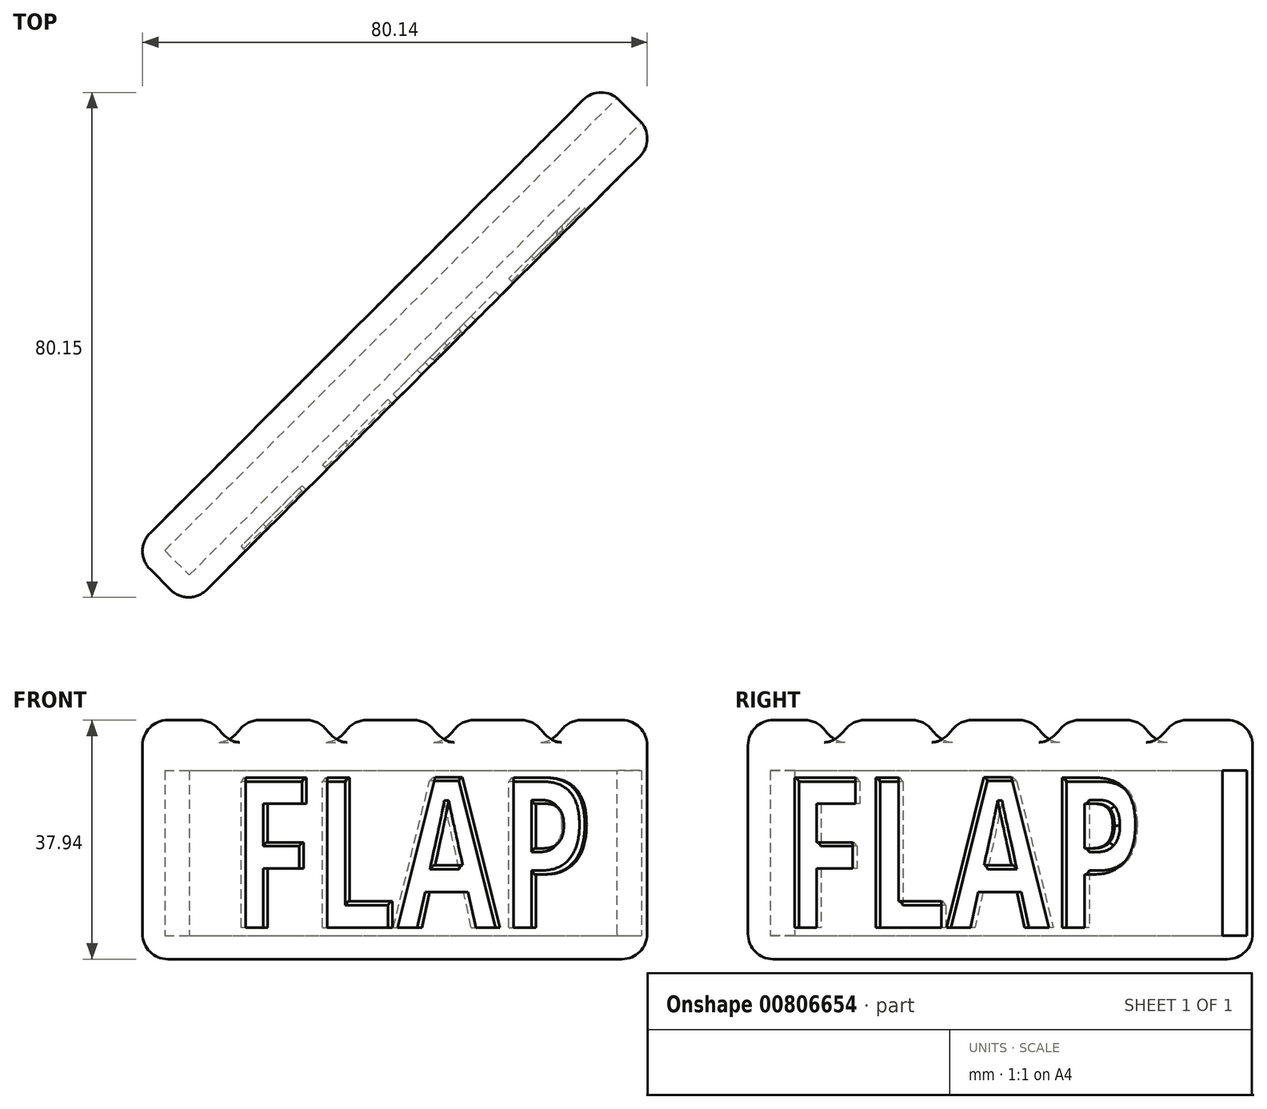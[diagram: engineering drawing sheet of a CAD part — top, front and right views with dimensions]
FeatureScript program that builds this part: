
annotation { "Feature Type Name" : "Feature", "Feature Type Description" : "" }
export const myFeature = defineFeature(function(context is Context, id is Id, definition is map)
    precondition{}
    {
        {
            assignVariable(context, id + "F0", {"name" : "tolerance", "anyValue" : 0.4 * mm});
        }
        {
            var Q0;
            Q0=qCreatedBy(makeId("Right.planeOp"),FACE);
            var sketch = newSketch(context, id + "F1", { "sketchPlane" : qUnion([Q0])});
            skLineSegment(sketch, "E0.bottom", {"start": v(0, 0) * mm, "end": v(152.4, 0) * mm});
            skLineSegment(sketch, "E0.top", {"start": v(0, 26.2) * mm, "end": v(152.4, 26.2) * mm});
            skLineSegment(sketch, "E0.left", {"start": v(0, 0) * mm, "end": v(0, 26.2) * mm});
            skLineSegment(sketch, "E0.right", {"start": v(152.4, 0) * mm, "end": v(152.4, 26.2) * mm});
            skSolve(sketch);
        }
        {
            var Q0;
            Q0=makeQuery(id+"F1.imprint","IMPRINT",FACE,{"disambiguationData":[TD([[makeQuery(id+"F1.imprint","IMPRINT",EDGE,{"derivedFrom":sQuery(id+"F1.wireOp",EDGE,"E0.bottom")}),1.0]])]});
            extrude(context, id + "F2", {"entities" : qUnion([Q0]), "endBound" : BoundingType.SYMMETRIC, "depth" : 4.7 * mm + 2 * getVariable(context, 'tolerance'), "offsetDistance" : 25.4 * mm});
        }
        {
            var Q0;
            Q0=qCreatedBy(makeId("Right.planeOp"),FACE);
            var sketch = newSketch(context, id + "F3", { "sketchPlane" : qUnion([Q0])});
            skLineSegment(sketch, "E1.bottom", {"start": v(-3.73, 29.95) * mm, "end": v(101.6, 29.95) * mm});
            skLineSegment(sketch, "E1.right", {"start": v(101.6, 29.95) * mm, "end": v(101.6, -8) * mm});
            skLineSegment(sketch, "E2.0.0", {"start": v(152.4, 26.2) * mm, "end": v(0, 26.2) * mm, "construction": true});
            skLineSegment(sketch, "E2.0.1", {"start": v(0, 26.2) * mm, "end": v(0, 0) * mm, "construction": true});
            skLineSegment(sketch, "E2.0.2", {"start": v(0, 0) * mm, "end": v(152.4, 0) * mm, "construction": true});
            skLineSegment(sketch, "E2.0.3", {"start": v(152.4, 0) * mm, "end": v(152.4, 26.2) * mm, "construction": true});
            skLineSegment(sketch, "E3", {"start": v(-3.73, 29.95) * mm, "end": v(-3.73, -8) * mm});
            skLineSegment(sketch, "E4", {"start": v(-3.73, -8) * mm, "end": v(4.36, -8) * mm});
            skLineSegment(sketch, "E5", {"start": v(-3.73, -14) * mm, "end": v(101.6, -14) * mm, "construction": true});
            skArc(sketch, "E6.1.0.0", {"start": v(43.26, -8) * mm, "mid": v(35.86, -4.47) * mm, "end": v(28.46, -8) * mm});
            skLineSegment(sketch, "E6.1.0.1", {"start": v(20.37, -14) * mm, "end": v(125.7, -14) * mm, "construction": true});
            skArc(sketch, "E6.2.0.0", {"start": v(67.36, -8) * mm, "mid": v(59.96, -4.47) * mm, "end": v(52.56, -8) * mm});
            skLineSegment(sketch, "E6.2.0.1", {"start": v(44.47, -14) * mm, "end": v(149.8, -14) * mm, "construction": true});
            skArc(sketch, "E6.3.0.0", {"start": v(91.46, -8) * mm, "mid": v(84.06, -4.47) * mm, "end": v(76.66, -8) * mm});
            skLineSegment(sketch, "E6.3.0.1", {"start": v(68.57, -14) * mm, "end": v(173.9, -14) * mm, "construction": true});
            skLineSegment(sketch, "E6.direction1", {"start": v(11.76, -14) * mm, "end": v(35.86, -14) * mm, "construction": true});
            skArc(sketch, "E7.trimOffspring", {"start": v(19.16, -8) * mm, "mid": v(11.76, -4.48) * mm, "end": v(4.36, -8) * mm});
            skLineSegment(sketch, "E8.trimOffspring", {"start": v(19.16, -8) * mm, "end": v(28.46, -8) * mm});
            skLineSegment(sketch, "E9.trimOffspring", {"start": v(43.26, -8) * mm, "end": v(52.56, -8) * mm});
            skLineSegment(sketch, "E10.trimOffspring", {"start": v(91.46, -8) * mm, "end": v(101.6, -8) * mm});
            skLineSegment(sketch, "E11.trimOffspring", {"start": v(67.36, -8) * mm, "end": v(76.66, -8) * mm});
            skSolve(sketch);
        }
        {
            var Q0;
            Q0=makeQuery(id+"F3.imprint","IMPRINT",FACE,{"disambiguationData":[TD([[makeQuery(id+"F3.imprint","IMPRINT",EDGE,{"derivedFrom":sQuery(id+"F3.wireOp",EDGE,"E1.bottom")}),-1.0]])]});
            extrude(context, id + "F4", {"entities" : qUnion([Q0]), "endBound" : BoundingType.SYMMETRIC, "depth" : 12.7 * mm, "offsetDistance" : 25.4 * mm});
        }
        {
            var Q0;
            {var subQ0=sQuery(id+"F3.wireOp",EDGE,"E1.top");Q0=makeQuery(id+"F4.opExtrude","SWEPT_FACE",FACE,{"disambiguationData":[OSD([subQ0]),TDD([makeQuery(id+"F3.imprint","IMPRINT",EDGE,{"disambiguationData":[TD([[makeQuery(id+"F3.imprint","INTERSECT",VERTEX,{"disambiguationData":[OD(0.0)],"derivedFrom":[subQ0,sQuery(id+"F3.wireOp",EDGE,"ST85VybC-jDZY-28ir-gOz5-esfVJcpXRgd0")]}),-1.0]])],"derivedFrom":subQ0})])]});}
            var Q1;
            {var subQ0=sQuery(id+"F3.wireOp",EDGE,"E1.top");Q1=makeQuery(id+"F4.opExtrude","SWEPT_FACE",FACE,{"disambiguationData":[OSD([subQ0]),TDD([makeQuery(id+"F3.imprint","IMPRINT",EDGE,{"disambiguationData":[TD([[makeQuery(id+"F3.imprint","INTERSECT",VERTEX,{"disambiguationData":[OD(0.0)],"derivedFrom":[subQ0,sQuery(id+"F3.wireOp",EDGE,"1f6f91a6-61ac-4653-8395-83e8434b74c3.1.0.0")]}),-1.0]])],"derivedFrom":subQ0})])]});}
            var Q2;
            {var subQ0=sQuery(id+"F3.wireOp",EDGE,"E1.top");Q2=makeQuery(id+"F4.opExtrude","SWEPT_FACE",FACE,{"disambiguationData":[OSD([subQ0]),TDD([makeQuery(id+"F3.imprint","IMPRINT",EDGE,{"disambiguationData":[TD([[makeQuery(id+"F3.imprint","INTERSECT",VERTEX,{"disambiguationData":[OD(0.0)],"derivedFrom":[subQ0,sQuery(id+"F3.wireOp",EDGE,"1f6f91a6-61ac-4653-8395-83e8434b74c3.2.0.0")]}),-1.0]])],"derivedFrom":subQ0})])]});}
            var Q3;
            Q3=makeQuery(id+"F4.opExtrude","SWEPT_FACE",FACE,{"disambiguationData":[OSD([sQuery(id+"F3.wireOp",EDGE,"1f6f91a6-61ac-4653-8395-83e8434b74c3.3.0.0")])]});
            var Q4;
            Q4=makeQuery(id+"F4.opExtrude","SWEPT_FACE",FACE,{"disambiguationData":[OSD([sQuery(id+"F3.wireOp",EDGE,"1f6f91a6-61ac-4653-8395-83e8434b74c3.2.0.0")])]});
            var Q5;
            Q5=makeQuery(id+"F4.opExtrude","SWEPT_FACE",FACE,{"disambiguationData":[OSD([sQuery(id+"F3.wireOp",EDGE,"1f6f91a6-61ac-4653-8395-83e8434b74c3.1.0.0")])]});
            var Q6;
            Q6=makeQuery(id+"F4.opExtrude","SWEPT_FACE",FACE,{"disambiguationData":[OSD([sQuery(id+"F3.wireOp",EDGE,"ST85VybC-jDZY-28ir-gOz5-esfVJcpXRgd0")])]});
            var Q7;
            {var subQ0=sQuery(id+"F3.wireOp",EDGE,"E1.top");Q7=makeQuery(id+"F4.opExtrude","SWEPT_FACE",FACE,{"disambiguationData":[OSD([subQ0]),TDD([makeQuery(id+"F3.imprint","IMPRINT",EDGE,{"disambiguationData":[TD([[makeQuery(id+"F3.imprint","INTERSECT",VERTEX,{"derivedFrom":[subQ0,sQuery(id+"F3.wireOp",EDGE,"E1.left")]}),-1.0]])],"derivedFrom":subQ0})])]});}
            var Q8;
            {var subQ0=sQuery(id+"F3.wireOp",EDGE,"E1.top");Q8=makeQuery(id+"F4.opExtrude","SWEPT_FACE",FACE,{"disambiguationData":[OSD([subQ0]),TDD([makeQuery(id+"F3.imprint","IMPRINT",EDGE,{"disambiguationData":[TD([[makeQuery(id+"F3.imprint","INTERSECT",VERTEX,{"derivedFrom":[subQ0,sQuery(id+"F3.wireOp",EDGE,"E1.right")]}),1.0]])],"derivedFrom":subQ0})])]});}
            var Q9;
            Q9=makeQuery(id+"F4.opExtrude","SWEPT_FACE",FACE,{"disambiguationData":[OSD([sQuery(id+"F3.wireOp",EDGE,"E1.left")])]});
            var Q10;
            Q10=makeQuery(id+"F4.opExtrude","SWEPT_FACE",FACE,{"disambiguationData":[OSD([sQuery(id+"F3.wireOp",EDGE,"E1.bottom")])]});
            var Q11;
            Q11=makeQuery(id+"F4.opExtrude","SWEPT_FACE",FACE,{"disambiguationData":[OSD([sQuery(id+"F3.wireOp",EDGE,"E1.right")])]});
            var Q12;
            Q12=makeQuery(id+"F4.opExtrude","SWEPT_EDGE",EDGE,{"disambiguationData":[OSD([sQuery(id+"F3.wireOp",EDGE,"E6.3.0.0"),sQuery(id+"F3.wireOp",EDGE,"E10.trimOffspring")])]});
            var Q13;
            Q13=makeQuery(id+"F4.opExtrude","SWEPT_EDGE",EDGE,{"disambiguationData":[OSD([sQuery(id+"F3.wireOp",EDGE,"E6.3.0.0"),sQuery(id+"F3.wireOp",EDGE,"E11.trimOffspring")])]});
            var Q14;
            Q14=makeQuery(id+"F4.opExtrude","SWEPT_EDGE",EDGE,{"disambiguationData":[OSD([sQuery(id+"F3.wireOp",EDGE,"E6.2.0.0"),sQuery(id+"F3.wireOp",EDGE,"E11.trimOffspring")])]});
            var Q15;
            Q15=makeQuery(id+"F4.opExtrude","SWEPT_EDGE",EDGE,{"disambiguationData":[OSD([sQuery(id+"F3.wireOp",EDGE,"E6.2.0.0"),sQuery(id+"F3.wireOp",EDGE,"E9.trimOffspring")])]});
            var Q16;
            Q16=makeQuery(id+"F4.opExtrude","SWEPT_EDGE",EDGE,{"disambiguationData":[OSD([sQuery(id+"F3.wireOp",EDGE,"E6.1.0.0"),sQuery(id+"F3.wireOp",EDGE,"E9.trimOffspring")])]});
            var Q17;
            Q17=makeQuery(id+"F4.opExtrude","SWEPT_EDGE",EDGE,{"disambiguationData":[OSD([sQuery(id+"F3.wireOp",EDGE,"E6.1.0.0"),sQuery(id+"F3.wireOp",EDGE,"E8.trimOffspring")])]});
            var Q18;
            Q18=makeQuery(id+"F4.opExtrude","SWEPT_EDGE",EDGE,{"disambiguationData":[OSD([sQuery(id+"F3.wireOp",EDGE,"E7.trimOffspring"),sQuery(id+"F3.wireOp",EDGE,"E8.trimOffspring")])]});
            var Q19;
            Q19=makeQuery(id+"F4.opExtrude","SWEPT_EDGE",EDGE,{"disambiguationData":[OSD([sQuery(id+"F3.wireOp",EDGE,"E4"),sQuery(id+"F3.wireOp",EDGE,"E7.trimOffspring")])]});
            var Q20;
            Q20=makeQuery(id+"F4.opExtrude","CAP_EDGE",EDGE,{"disambiguationData":[OSD([sQuery(id+"F3.wireOp",EDGE,"E7.trimOffspring")])],"isStart":false});
            var Q21;
            Q21=makeQuery(id+"F4.opExtrude","CAP_EDGE",EDGE,{"disambiguationData":[OSD([sQuery(id+"F3.wireOp",EDGE,"E6.1.0.0")])],"isStart":false});
            var Q22;
            Q22=makeQuery(id+"F4.opExtrude","CAP_EDGE",EDGE,{"disambiguationData":[OSD([sQuery(id+"F3.wireOp",EDGE,"E6.2.0.0")])],"isStart":false});
            var Q23;
            Q23=makeQuery(id+"F4.opExtrude","CAP_EDGE",EDGE,{"disambiguationData":[OSD([sQuery(id+"F3.wireOp",EDGE,"E6.3.0.0")])],"isStart":false});
            var Q24;
            Q24=makeQuery(id+"F4.opExtrude","CAP_EDGE",EDGE,{"disambiguationData":[OSD([sQuery(id+"F3.wireOp",EDGE,"E6.3.0.0")])],"isStart":true});
            var Q25;
            Q25=makeQuery(id+"F4.opExtrude","CAP_EDGE",EDGE,{"disambiguationData":[OSD([sQuery(id+"F3.wireOp",EDGE,"E6.2.0.0")])],"isStart":true});
            var Q26;
            Q26=makeQuery(id+"F4.opExtrude","CAP_EDGE",EDGE,{"disambiguationData":[OSD([sQuery(id+"F3.wireOp",EDGE,"E10.trimOffspring")])],"isStart":true});
            var Q27;
            Q27=makeQuery(id+"F4.opExtrude","CAP_EDGE",EDGE,{"disambiguationData":[OSD([sQuery(id+"F3.wireOp",EDGE,"E9.trimOffspring")])],"isStart":true});
            var Q28;
            Q28=makeQuery(id+"F4.opExtrude","CAP_EDGE",EDGE,{"disambiguationData":[OSD([sQuery(id+"F3.wireOp",EDGE,"E6.1.0.0")])],"isStart":true});
            var Q29;
            Q29=makeQuery(id+"F4.opExtrude","CAP_EDGE",EDGE,{"disambiguationData":[OSD([sQuery(id+"F3.wireOp",EDGE,"E8.trimOffspring")])],"isStart":true});
            var Q30;
            Q30=makeQuery(id+"F4.opExtrude","CAP_EDGE",EDGE,{"disambiguationData":[OSD([sQuery(id+"F3.wireOp",EDGE,"E7.trimOffspring")])],"isStart":true});
            var Q31;
            Q31=makeQuery(id+"F4.opExtrude","CAP_EDGE",EDGE,{"disambiguationData":[OSD([sQuery(id+"F3.wireOp",EDGE,"E4")])],"isStart":true});
            var Q32;
            Q32=makeQuery(id+"F4.opExtrude","CAP_EDGE",EDGE,{"disambiguationData":[OSD([sQuery(id+"F3.wireOp",EDGE,"E11.trimOffspring")])],"isStart":true});
            var Q33;
            Q33=makeQuery(id+"F4.opExtrude","CAP_EDGE",EDGE,{"disambiguationData":[OSD([sQuery(id+"F3.wireOp",EDGE,"E11.trimOffspring")])],"isStart":false});
            var Q34;
            Q34=makeQuery(id+"F4.opExtrude","CAP_EDGE",EDGE,{"disambiguationData":[OSD([sQuery(id+"F3.wireOp",EDGE,"E9.trimOffspring")])],"isStart":false});
            var Q35;
            Q35=makeQuery(id+"F4.opExtrude","CAP_EDGE",EDGE,{"disambiguationData":[OSD([sQuery(id+"F3.wireOp",EDGE,"E8.trimOffspring")])],"isStart":false});
            var Q36;
            Q36=makeQuery(id+"F4.opExtrude","CAP_EDGE",EDGE,{"disambiguationData":[OSD([sQuery(id+"F3.wireOp",EDGE,"E4")])],"isStart":false});
            var Q37;
            Q37=makeQuery(id+"F4.opExtrude","CAP_EDGE",EDGE,{"disambiguationData":[OSD([sQuery(id+"F3.wireOp",EDGE,"E10.trimOffspring")])],"isStart":false});
            var Q38;
            Q38=makeQuery(id+"F4.opExtrude","SWEPT_EDGE",EDGE,{"disambiguationData":[OSD([sQuery(id+"F3.wireOp",EDGE,"E3"),sQuery(id+"F3.wireOp",EDGE,"E4")])]});
            var Q39;
            Q39=makeQuery(id+"F4.opExtrude","CAP_EDGE",EDGE,{"disambiguationData":[OSD([sQuery(id+"F3.wireOp",EDGE,"E3")])],"isStart":true});
            var Q40;
            Q40=makeQuery(id+"F4.opExtrude","CAP_EDGE",EDGE,{"disambiguationData":[OSD([sQuery(id+"F3.wireOp",EDGE,"E3")])],"isStart":false});
            fillet(context, id + "F5", {"entities" : qUnion([Q0, Q1, Q2, Q3, Q4, Q5, Q6, Q7, Q8, Q9, Q10, Q11, Q12, Q13, Q14, Q15, Q16, Q17, Q18, Q19, Q20, Q21, Q22, Q23, Q24, Q25, Q26, Q27, Q28, Q29, Q30, Q31, Q32, Q33, Q34, Q35, Q36, Q37, Q38, Q39, Q40]), "radius" : 4 * mm, "tangentPropagation" : true, "allowEdgeOverflow" : false});
        }
        {
            var Q0;
            Q0=makeQuery(id+"F2.opExtrude","SWEPT_BODY",BODY,{"disambiguationData":[OSD([sQuery(id+"F1.wireOp",EDGE,"E0.bottom"),sQuery(id+"F1.wireOp",EDGE,"E0.top"),sQuery(id+"F1.wireOp",EDGE,"E0.left"),sQuery(id+"F1.wireOp",EDGE,"E0.right")])]});
            var Q1;
            Q1=makeQuery(id+"F4.opExtrude","SWEPT_BODY",BODY,{"disambiguationData":[OSD([sQuery(id+"F3.wireOp",EDGE,"E1.bottom"),sQuery(id+"F3.wireOp",EDGE,"E1.top"),sQuery(id+"F3.wireOp",EDGE,"E1.left"),sQuery(id+"F3.wireOp",EDGE,"E1.right"),sQuery(id+"F3.wireOp",EDGE,"ST85VybC-jDZY-28ir-gOz5-esfVJcpXRgd0"),sQuery(id+"F3.wireOp",EDGE,"1f6f91a6-61ac-4653-8395-83e8434b74c3.1.0.0"),sQuery(id+"F3.wireOp",EDGE,"1f6f91a6-61ac-4653-8395-83e8434b74c3.2.0.0"),sQuery(id+"F3.wireOp",EDGE,"1f6f91a6-61ac-4653-8395-83e8434b74c3.3.0.0")])]});
            booleanBodies(context, id + "F6", {"operationType" : BooleanOperationType.SUBTRACTION, "tools" : qUnion([Q0]), "targets" : qUnion([Q1])});
        }
        {
            var Q0;
            Q0=makeQuery(id+"F4.opExtrude","CAP_FACE",FACE,{"disambiguationData":[OSD([sQuery(id+"F3.wireOp",EDGE,"E1.bottom"),sQuery(id+"F3.wireOp",EDGE,"E1.right"),sQuery(id+"F3.wireOp",EDGE,"E3"),sQuery(id+"F3.wireOp",EDGE,"E4"),sQuery(id+"F3.wireOp",EDGE,"E6.1.0.0"),sQuery(id+"F3.wireOp",EDGE,"E6.2.0.0"),sQuery(id+"F3.wireOp",EDGE,"E6.3.0.0"),sQuery(id+"F3.wireOp",EDGE,"E7.trimOffspring"),sQuery(id+"F3.wireOp",EDGE,"E8.trimOffspring"),sQuery(id+"F3.wireOp",EDGE,"E9.trimOffspring"),sQuery(id+"F3.wireOp",EDGE,"E10.trimOffspring"),sQuery(id+"F3.wireOp",EDGE,"E11.trimOffspring")])],"isStart":true});
            var sketch = newSketch(context, id + "F7", { "sketchPlane" : qUnion([Q0])});
            skText(sketch, "E12", { "text": "FLAP", "fontName": "OpenSans-Bold.ttf"});
            skPoint(sketch, "E13", {"position": v(-59.96, 12.74) * mm});
            skPoint(sketch, "E14", {"position": v(-46.93, 12.95) * mm});
            const initialGuessF7  = {"E12": [-0.00607, 0.02495, -1, 0, 0.024]};
            skSetInitialGuess(sketch, initialGuessF7);
            skSolve(sketch);
        }
        {
            var Q0;
            Q0 = qSketchRegion(id + "F7", true);
            extrude(context, id + "F8", {"entities" : qUnion([Q0]), "operationType" : NewBodyOperationType.REMOVE, "oppositeDirection" : true, "depth" : 1 * mm, "offsetDistance" : 25 * mm});
        }
        {
            var Q0;
            Q0=makeQuery(id+"F8.boolean.opBoolean","COPY",EDGE,{"derivedFrom":makeQuery(id+"F8.opExtrude","CAP_EDGE",EDGE,{"disambiguationData":[OSD([sQuery(id+"F7.wireOp",EDGE,"E12.sketch_text.stroke-27")])],"isStart":false})});
            var Q1;
            Q1=makeQuery(id+"F8.boolean.opBoolean","COPY",EDGE,{"derivedFrom":makeQuery(id+"F8.opExtrude","CAP_EDGE",EDGE,{"disambiguationData":[OSD([sQuery(id+"F7.wireOp",EDGE,"E12.sketch_text.stroke-29")])],"isStart":false})});
            var Q2;
            Q2=makeQuery(id+"F8.boolean.opBoolean","COPY",EDGE,{"derivedFrom":makeQuery(id+"F8.opExtrude","CAP_EDGE",EDGE,{"disambiguationData":[OSD([sQuery(id+"F7.wireOp",EDGE,"E12.sketch_text.stroke-11")])],"isStart":false})});
            var Q3;
            Q3=makeQuery(id+"F8.boolean.opBoolean","COPY",EDGE,{"derivedFrom":makeQuery(id+"F8.opExtrude","CAP_EDGE",EDGE,{"disambiguationData":[OSD([sQuery(id+"F7.wireOp",EDGE,"E12.sketch_text.stroke-21")])],"isStart":false})});
            var Q4;
            Q4=makeQuery(id+"F8.boolean.opBoolean","COPY",EDGE,{"derivedFrom":makeQuery(id+"F8.opExtrude","CAP_EDGE",EDGE,{"disambiguationData":[OSD([sQuery(id+"F7.wireOp",EDGE,"E12.sketch_text.stroke-41")])],"isStart":false})});
            var Q5;
            Q5=makeQuery(id+"F8.boolean.opBoolean","COPY",EDGE,{"derivedFrom":makeQuery(id+"F8.opExtrude","CAP_EDGE",EDGE,{"disambiguationData":[OSD([sQuery(id+"F7.wireOp",EDGE,"E12.sketch_text.stroke-2")])],"isStart":false})});
            var Q6;
            Q6=makeQuery(id+"F8.boolean.opBoolean","COPY",EDGE,{"derivedFrom":makeQuery(id+"F8.opExtrude","CAP_EDGE",EDGE,{"disambiguationData":[OSD([sQuery(id+"F7.wireOp",EDGE,"E12.sketch_text.stroke-6")])],"isStart":false})});
            var Q7;
            Q7=makeQuery(id+"F8.boolean.opBoolean","COPY",EDGE,{"derivedFrom":makeQuery(id+"F8.opExtrude","CAP_EDGE",EDGE,{"disambiguationData":[OSD([sQuery(id+"F7.wireOp",EDGE,"E12.sketch_text.stroke-13")])],"isStart":false})});
            chamfer(context, id + "F9", {"entities" : qUnion([Q0, Q1, Q2, Q3, Q4, Q5, Q6, Q7]), "width" : .6 * mm, "tangentPropagation" : true});
        }
        {
            var Q0;
            Q0=makeQuery(id+"F4.opExtrude","SWEPT_BODY",BODY,{"disambiguationData":[OSD([sQuery(id+"F3.wireOp",EDGE,"E1.bottom"),sQuery(id+"F3.wireOp",EDGE,"E1.top"),sQuery(id+"F3.wireOp",EDGE,"E1.left"),sQuery(id+"F3.wireOp",EDGE,"E1.right"),sQuery(id+"F3.wireOp",EDGE,"ST85VybC-jDZY-28ir-gOz5-esfVJcpXRgd0"),sQuery(id+"F3.wireOp",EDGE,"1f6f91a6-61ac-4653-8395-83e8434b74c3.1.0.0"),sQuery(id+"F3.wireOp",EDGE,"1f6f91a6-61ac-4653-8395-83e8434b74c3.2.0.0"),sQuery(id+"F3.wireOp",EDGE,"1f6f91a6-61ac-4653-8395-83e8434b74c3.3.0.0"),sQuery(id+"F3.wireOp",EDGE,"8d30070c-a4d7-41d9-b422-1acecc7076d4.sketch_text.stroke-0"),sQuery(id+"F3.wireOp",EDGE,"8d30070c-a4d7-41d9-b422-1acecc7076d4.sketch_text.stroke-1"),sQuery(id+"F3.wireOp",EDGE,"8d30070c-a4d7-41d9-b422-1acecc7076d4.sketch_text.stroke-2"),sQuery(id+"F3.wireOp",EDGE,"8d30070c-a4d7-41d9-b422-1acecc7076d4.sketch_text.stroke-3"),sQuery(id+"F3.wireOp",EDGE,"8d30070c-a4d7-41d9-b422-1acecc7076d4.sketch_text.stroke-4"),sQuery(id+"F3.wireOp",EDGE,"8d30070c-a4d7-41d9-b422-1acecc7076d4.sketch_text.stroke-5"),sQuery(id+"F3.wireOp",EDGE,"8d30070c-a4d7-41d9-b422-1acecc7076d4.sketch_text.stroke-6"),sQuery(id+"F3.wireOp",EDGE,"8d30070c-a4d7-41d9-b422-1acecc7076d4.sketch_text.stroke-7"),sQuery(id+"F3.wireOp",EDGE,"8d30070c-a4d7-41d9-b422-1acecc7076d4.sketch_text.stroke-8"),sQuery(id+"F3.wireOp",EDGE,"8d30070c-a4d7-41d9-b422-1acecc7076d4.sketch_text.stroke-9"),sQuery(id+"F3.wireOp",EDGE,"8d30070c-a4d7-41d9-b422-1acecc7076d4.sketch_text.stroke-10"),sQuery(id+"F3.wireOp",EDGE,"8d30070c-a4d7-41d9-b422-1acecc7076d4.sketch_text.stroke-11"),sQuery(id+"F3.wireOp",EDGE,"8d30070c-a4d7-41d9-b422-1acecc7076d4.sketch_text.stroke-12"),sQuery(id+"F3.wireOp",EDGE,"8d30070c-a4d7-41d9-b422-1acecc7076d4.sketch_text.stroke-13"),sQuery(id+"F3.wireOp",EDGE,"8d30070c-a4d7-41d9-b422-1acecc7076d4.sketch_text.stroke-14"),sQuery(id+"F3.wireOp",EDGE,"8d30070c-a4d7-41d9-b422-1acecc7076d4.sketch_text.stroke-15"),sQuery(id+"F3.wireOp",EDGE,"8d30070c-a4d7-41d9-b422-1acecc7076d4.sketch_text.stroke-16"),sQuery(id+"F3.wireOp",EDGE,"8d30070c-a4d7-41d9-b422-1acecc7076d4.sketch_text.stroke-17"),sQuery(id+"F3.wireOp",EDGE,"8d30070c-a4d7-41d9-b422-1acecc7076d4.sketch_text.stroke-18"),sQuery(id+"F3.wireOp",EDGE,"8d30070c-a4d7-41d9-b422-1acecc7076d4.sketch_text.stroke-19"),sQuery(id+"F3.wireOp",EDGE,"8d30070c-a4d7-41d9-b422-1acecc7076d4.sketch_text.stroke-20"),sQuery(id+"F3.wireOp",EDGE,"8d30070c-a4d7-41d9-b422-1acecc7076d4.sketch_text.stroke-21"),sQuery(id+"F3.wireOp",EDGE,"8d30070c-a4d7-41d9-b422-1acecc7076d4.sketch_text.stroke-22"),sQuery(id+"F3.wireOp",EDGE,"8d30070c-a4d7-41d9-b422-1acecc7076d4.sketch_text.stroke-23"),sQuery(id+"F3.wireOp",EDGE,"8d30070c-a4d7-41d9-b422-1acecc7076d4.sketch_text.stroke-35"),sQuery(id+"F3.wireOp",EDGE,"8d30070c-a4d7-41d9-b422-1acecc7076d4.sketch_text.stroke-36"),sQuery(id+"F3.wireOp",EDGE,"8d30070c-a4d7-41d9-b422-1acecc7076d4.sketch_text.stroke-37"),sQuery(id+"F3.wireOp",EDGE,"8d30070c-a4d7-41d9-b422-1acecc7076d4.sketch_text.stroke-38"),sQuery(id+"F3.wireOp",EDGE,"8d30070c-a4d7-41d9-b422-1acecc7076d4.sketch_text.stroke-39"),sQuery(id+"F3.wireOp",EDGE,"8d30070c-a4d7-41d9-b422-1acecc7076d4.sketch_text.stroke-40"),sQuery(id+"F3.wireOp",EDGE,"8d30070c-a4d7-41d9-b422-1acecc7076d4.sketch_text.stroke-41"),sQuery(id+"F3.wireOp",EDGE,"8d30070c-a4d7-41d9-b422-1acecc7076d4.sketch_text.stroke-42"),sQuery(id+"F3.wireOp",EDGE,"8d30070c-a4d7-41d9-b422-1acecc7076d4.sketch_text.stroke-43")])]});
            var Q1;
            Q1=sQuery(id+"F3.wireOp",EDGE,"E1.bottom");
            transform(context, id + "F10", {"entities" : qUnion([Q0]), "transformType" : TransformType.ROTATION, "transformAxis" : qUnion([Q1]), "angle" : 180 * degree, "makeCopy" : false});
        }
        {
            var Q0;
            Q0=makeQuery(id+"F4.opExtrude","SWEPT_BODY",BODY,{"disambiguationData":[OSD([sQuery(id+"F3.wireOp",EDGE,"E1.bottom"),sQuery(id+"F3.wireOp",EDGE,"E1.right"),sQuery(id+"F3.wireOp",EDGE,"E3"),sQuery(id+"F3.wireOp",EDGE,"E4"),sQuery(id+"F3.wireOp",EDGE,"E6.1.0.0"),sQuery(id+"F3.wireOp",EDGE,"E6.2.0.0"),sQuery(id+"F3.wireOp",EDGE,"E6.3.0.0"),sQuery(id+"F3.wireOp",EDGE,"E7.trimOffspring"),sQuery(id+"F3.wireOp",EDGE,"E8.trimOffspring"),sQuery(id+"F3.wireOp",EDGE,"E9.trimOffspring"),sQuery(id+"F3.wireOp",EDGE,"E10.trimOffspring"),sQuery(id+"F3.wireOp",EDGE,"E11.trimOffspring")])]});
            var Q1;
            {var subQ0=sQuery(id+"F3.wireOp",EDGE,"E3");Q1=makeQuery(id+"F5.opFillet","BLEND_EDGE",EDGE,{"blendedFrom":[makeQuery(id+"F4.opExtrude","CAP_EDGE",EDGE,{"disambiguationData":[OSD([subQ0])],"isStart":false}),makeQuery(id+"F4.opExtrude","SWEPT_FACE",FACE,{"disambiguationData":[OSD([subQ0])]})],"blendedInto":[makeQuery(id+"F4.opExtrude","SWEPT_FACE",FACE,{"disambiguationData":[OSD([subQ0])]})]});}
            transform(context, id + "F11", {"entities" : qUnion([Q0]), "transformType" : TransformType.ROTATION, "transformAxis" : qUnion([Q1]), "angle" : 45 * degree, "oppositeDirection" : true, "makeCopy" : false});
        }
    });
